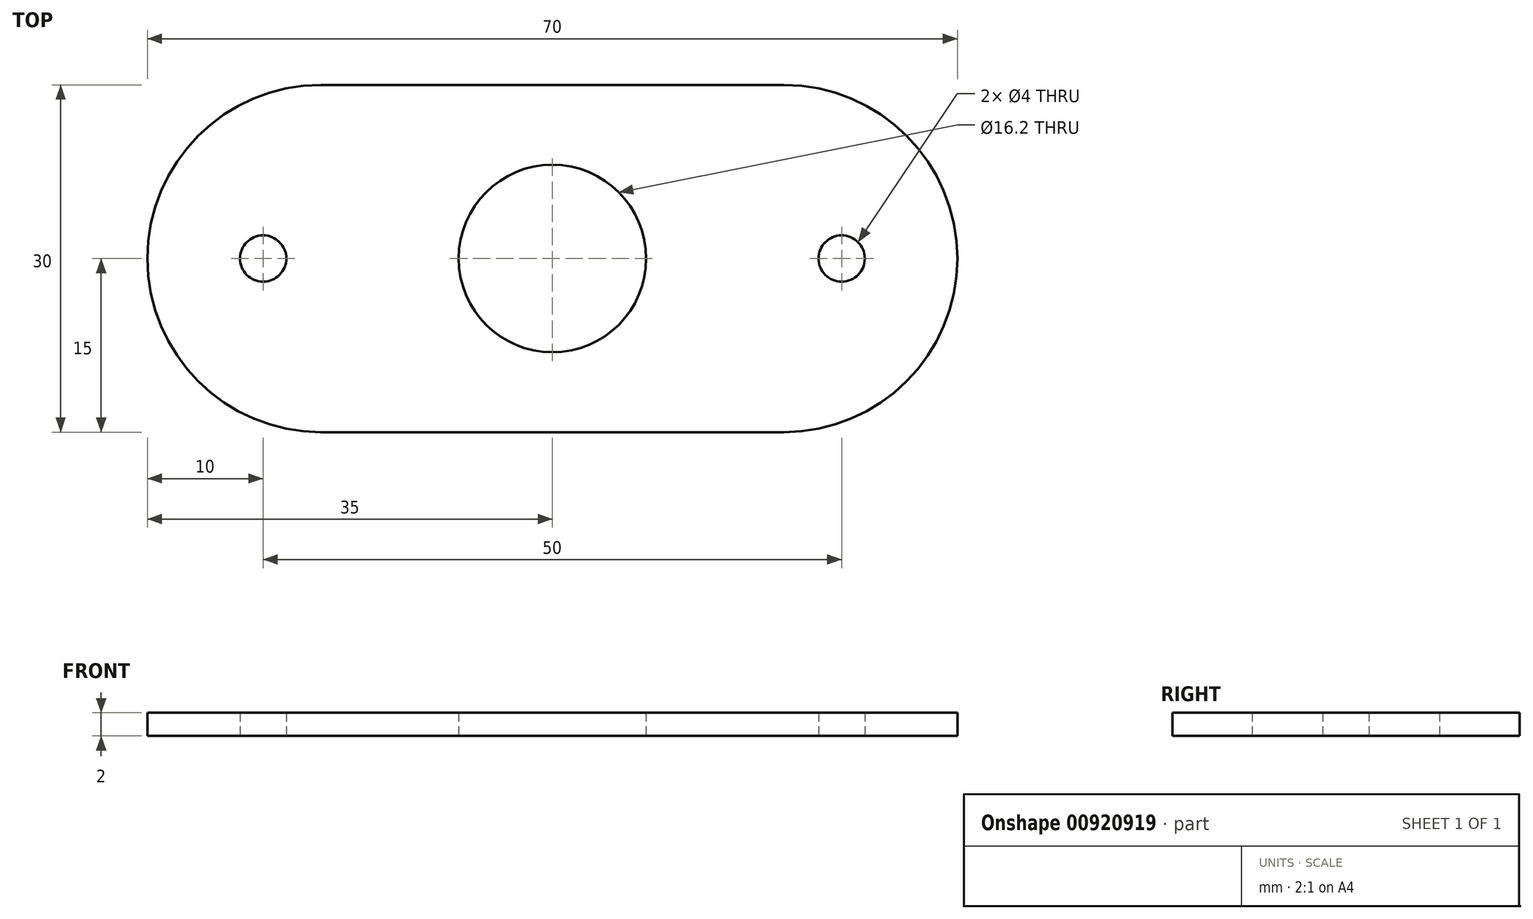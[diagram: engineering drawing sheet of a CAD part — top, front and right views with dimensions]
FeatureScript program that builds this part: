
annotation { "Feature Type Name" : "Feature", "Feature Type Description" : "" }
export const myFeature = defineFeature(function(context is Context, id is Id, definition is map)
    precondition{}
    {
        {
            var Q0;
            Q0=qCreatedBy(makeId("Top.planeOp"),FACE);
            var sketch = newSketch(context, id + "F0", { "sketchPlane" : qUnion([Q0])});
            skCircle(sketch, "E0", {"center": v(0, 0) * mm, "radius": 8.1 * mm});
            skLineSegment(sketch, "E1", {"start": v(-20, 0) * mm, "end": v(20, 0) * mm});
            skArc(sketch, "E2.0.startCap", {"start": v(-20, -15) * mm, "mid": v(-35, 0) * mm, "end": v(-20, 15) * mm});
            skArc(sketch, "E2.0.endCap", {"start": v(20, 15) * mm, "mid": v(35, 0) * mm, "end": v(20, -15) * mm});
            skLineSegment(sketch, "E2.0.left", {"start": v(-20, 15) * mm, "end": v(20, 15) * mm});
            skLineSegment(sketch, "E2.0.right", {"start": v(-20, -15) * mm, "end": v(20, -15) * mm});
            skCircle(sketch, "E3", {"center": v(-25, 0) * mm, "radius": 2 * mm});
            skCircle(sketch, "E4", {"center": v(25, 0) * mm, "radius": 2 * mm});
            skSolve(sketch);
        }
        {
            var Q0;
            Q0 = qSketchRegion(id + "F0", true);
            extrude(context, id + "F1", {"entities" : qUnion([Q0]), "depth" : 2 * mm, "offsetDistance" : 25 * mm});
        }
    });
